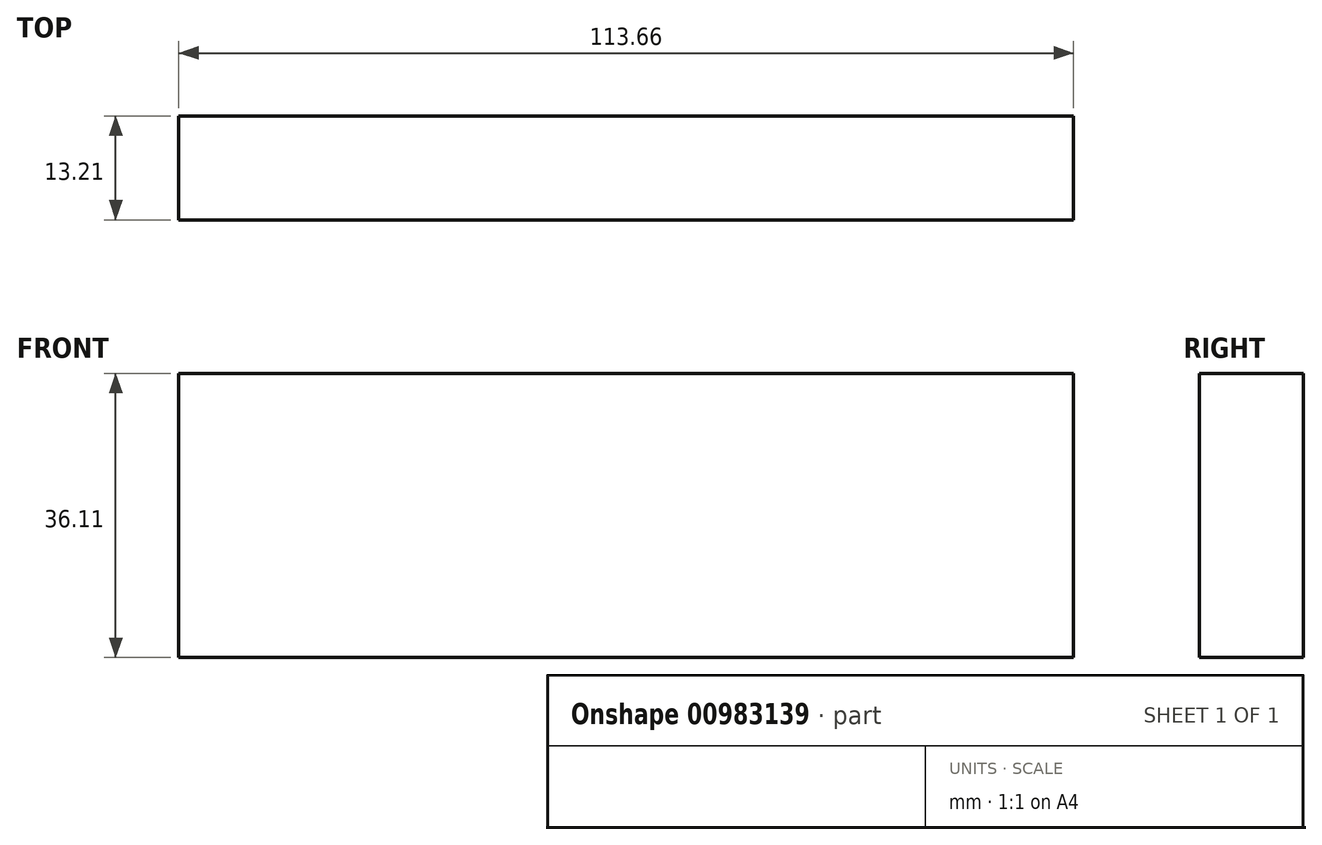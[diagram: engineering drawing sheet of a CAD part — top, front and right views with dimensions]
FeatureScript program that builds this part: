
annotation { "Feature Type Name" : "Feature", "Feature Type Description" : "" }
export const myFeature = defineFeature(function(context is Context, id is Id, definition is map)
    precondition{}
    {
        {
            var Q0;
            Q0=qCreatedBy(makeId("Front.planeOp"),FACE);
            var sketch = newSketch(context, id + "F0", { "sketchPlane" : qUnion([Q0])});
            skLineSegment(sketch, "E0.bottom", {"start": v(113.66, 12.23) * mm, "end": v(0, 12.23) * mm});
            skLineSegment(sketch, "E0.top", {"start": v(113.66, 48.34) * mm, "end": v(0, 48.34) * mm});
            skLineSegment(sketch, "E0.left", {"start": v(113.66, 12.23) * mm, "end": v(113.66, 48.34) * mm});
            skLineSegment(sketch, "E0.right", {"start": v(0, 12.23) * mm, "end": v(0, 48.34) * mm});
            skSolve(sketch);
        }
        {
            var Q0;
            Q0=makeQuery(id+"F0.imprint","IMPRINT",FACE,{"disambiguationData":[TD([[makeQuery(id+"F0.imprint","IMPRINT",EDGE,{"derivedFrom":sQuery(id+"F0.wireOp",EDGE,"E0.bottom")}),-1.0]])]});
            extrude(context, id + "F1", {"entities" : qUnion([Q0]), "depth" : 13.2 * mm, "offsetDistance" : 25.4 * mm});
        }
    });
